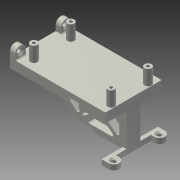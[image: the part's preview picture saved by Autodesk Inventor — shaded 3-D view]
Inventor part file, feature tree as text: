
AUTODESK INVENTOR PART (.ipt)
format: ipt  version: 2015 (Build 190159000, 159)  size: 358,400 bytes
history: native  units: mm
features: extrude x12, reference x12, sketch x11, hole x3, mirror x2, fillet x2, other x1, plane x1, projected_geometry x1
ambient origin geometry x8: Origin, YZ Plane, XZ Plane, XY Plane, X Axis, Y Axis, Z Axis, Center Point
bodies: Body1 (feature_tree)
feature tree (45):
  other  "Sólido1"
  sketch  "Boceto1"  dims[d1=27.0mm d3=32.0mm d4=0.0mm]
  extrude  "Extrusión1"  Depth=32.0mm TaperAngle=0.0deg
  extrude  "Extrusión2"  Depth=3.8mm TaperAngle=0.0deg
  plane  "Plano de trabajo1"
  extrude  "Extrusión3"  Depth=10.0mm
  sketch  "Boceto6"  dims[d25=3.0mm d26=0.0mm d38=10.0mm]
  extrude  "Extrusión7"  Depth=3.0mm TaperAngle=0.0deg
  extrude  "Extrusión8"  Depth=2.0mm
  extrude  "Extrusión10"  Depth=3.0mm
  hole  "Agujero2"  [1 undecoded]
  mirror  "Simetría1"
  extrude  "Extrusión9"  Depth=1.0mm
  fillet  "Empalme1"  Radius=2.0mm
  fillet  "Empalme2"  Radius=1.0mm
  extrude  "Extrusión12"  Depth=0.1mm
  extrude  "Extrusión11"  Depth=10.0mm
  mirror  "Simetría2"
  hole  "Agujero3"  [1 undecoded]
  hole  "Agujero4"  [1 undecoded]
  extrude  "Extrusión13"  Depth=3.0mm
  extrude  "Extrusión14"  Depth=10.0mm
  extrude  "Extrusión15"  Depth=10.0mm
  sketch  "Boceto2"  dims[d5=32.0mm d6=0.0mm d8=3.8mm d9=0.0mm]
  sketch  "Boceto7"  dims[d39=6.0mm d40=3.0mm d41=0.0mm]
  sketch  "Boceto8"  dims[d42=10.0mm d43=10.0mm]
  sketch  "Boceto9"  dims[d44=2.4mm d45=6.0mm d46=4.6mm d47=2.0mm d48=90.0deg d49=8.0mm d50=20.594885mm d51=0.2mm]
  projected_geometry  "Contorno proyectado2"
  reference  "Referencia6"
  reference  "Referencia7"
  sketch  "Boceto13"  dims[d53=1.0mm d54=1.0mm d55=1.0mm d56=1.0mm d58=3.0mm d59=0.0mm d60=3.0mm]
  reference  "Referencia15"
  reference  "Referencia16"
  sketch  "Boceto14"  dims[d61=3.0mm d62=3.0mm]
  reference  "Referencia17"
  reference  "Referencia18"
  sketch  "Boceto15"  dims[d68=1.0mm d69=1.0mm d70=2.0mm d71=1.0mm]
  reference  "Referencia19"
  reference  "Referencia20"
  reference  "Referencia21"
  reference  "Referencia22"
  reference  "Referencia23"
  sketch  "Boceto16"  dims[d89=0.1mm d93=0.1mm]
  reference  "Referencia24"
  sketch  "Boceto18"  dims[d95=0.1mm d97=0.1mm d98=0.1mm d104=53.0mm d105=10.0mm d106=0.0mm d107=3.0mm d109=10.0mm d110=10.0mm d111=0.1mm d112=10.0mm d113=0.0mm d114=10.0mm d115=0.0mm d116=0.8mm d117=10.0mm d118=10.0mm d119=2.4mm d120=6.0mm d121=4.0mm d122=2.0mm d123=90.0deg d124=8.0mm d125=20.594885mm d126=10.0mm d127=10.0mm d128=2.4mm d129=6.0mm d130=4.0mm d131=2.0mm d132=90.0deg d133=8.0mm d134=20.594885mm d135=0.5mm d136=0.5mm d137=0.5mm d138=0.5mm d139=8.5mm d140=0.0mm d141=0.65mm d142=0.65mm d143=0.65mm d144=0.65mm d145=10.0mm d146=0.0mm d150=1.7mm d151=10.0mm d152=0.0mm]
note: 3 required parameter values undecoded (feature->parameter linkage not recoverable at this tier; creation-order binding heuristic only, values carry confidence <= 0.55)
